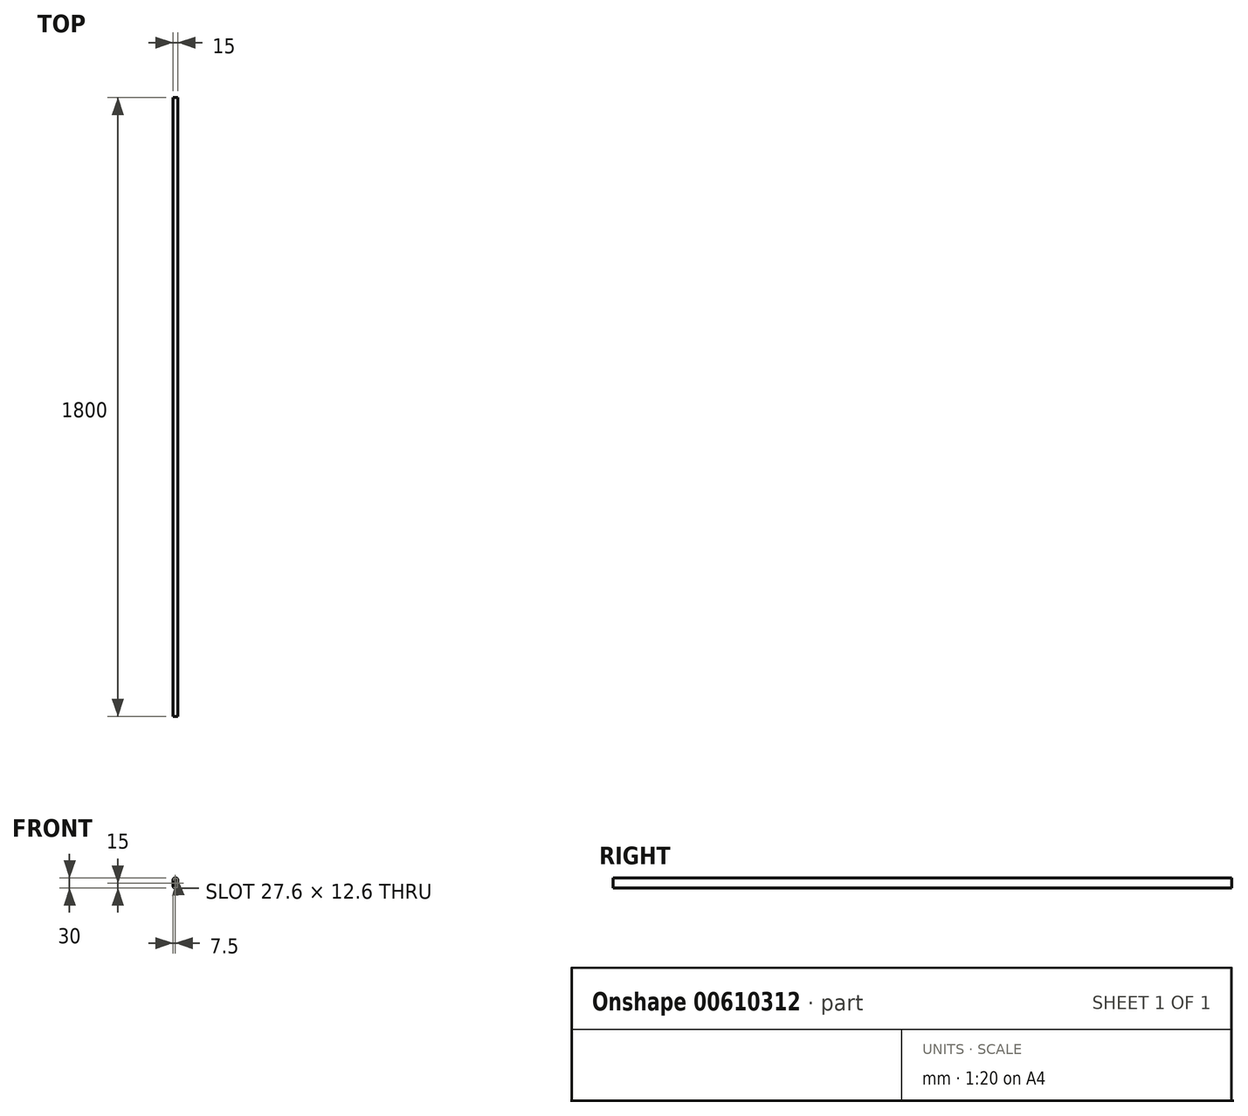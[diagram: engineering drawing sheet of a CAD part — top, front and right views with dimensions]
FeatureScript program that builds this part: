
annotation { "Feature Type Name" : "Feature", "Feature Type Description" : "" }
export const myFeature = defineFeature(function(context is Context, id is Id, definition is map)
    precondition{}
    {
        {
            var Q0;
            Q0=qCreatedBy(makeId("Front.planeOp"),FACE);
            var sketch = newSketch(context, id + "F0", { "sketchPlane" : qUnion([Q0])});
            skLineSegment(sketch, "E0.bottom", {"start": v(0, 15) * mm, "end": v(0, 15) * mm});
            skLineSegment(sketch, "E0.top", {"start": v(0, -15) * mm, "end": v(0, -15) * mm});
            skLineSegment(sketch, "E0.left", {"start": v(-7.5, 7.5) * mm, "end": v(-7.5, -7.5) * mm});
            skLineSegment(sketch, "E0.right", {"start": v(7.5, 7.5) * mm, "end": v(7.5, -7.5) * mm});
            skLineSegment(sketch, "E1", {"start": v(0, 0) * mm, "end": v(0, 15) * mm, "construction": true});
            skLineSegment(sketch, "E2", {"start": v(0, 0) * mm, "end": v(-7.5, 0) * mm, "construction": true});
            skPoint(sketch, "E3.visualSharp", {"position": v(-7.5, 15) * mm});
            skArc(sketch, "E3.filletArc", {"start": v(0, 15) * mm, "mid": v(-5.3, 12.8) * mm, "end": v(-7.5, 7.5) * mm});
            skPoint(sketch, "E4.visualSharp", {"position": v(7.5, 15) * mm});
            skArc(sketch, "E4.filletArc", {"start": v(7.5, 7.5) * mm, "mid": v(5.3, 12.8) * mm, "end": v(0, 15) * mm});
            skPoint(sketch, "E5.visualSharp", {"position": v(-7.5, -15) * mm});
            skArc(sketch, "E5.filletArc", {"start": v(-7.5, -7.5) * mm, "mid": v(-5.3, -12.8) * mm, "end": v(0, -15) * mm});
            skPoint(sketch, "E6.visualSharp", {"position": v(7.5, -15) * mm});
            skArc(sketch, "E6.filletArc", {"start": v(0, -15) * mm, "mid": v(5.3, -12.8) * mm, "end": v(7.5, -7.5) * mm});
            skSolve(sketch);
        }
        {
            var Q0;
            Q0=makeQuery(id+"F0.imprint","IMPRINT",FACE,{"disambiguationData":[TD([[makeQuery(id+"F0.imprint","IMPRINT",EDGE,{"derivedFrom":sQuery(id+"F0.wireOp",EDGE,"E1")}),1.0]])]});
            var Q1;
            Q1=makeQuery(id+"F0.imprint","IMPRINT",FACE,{"disambiguationData":[TD([[makeQuery(id+"F0.imprint","IMPRINT",EDGE,{"derivedFrom":sQuery(id+"F0.wireOp",EDGE,"E0.right")}),-1.0]])]});
            extrude(context, id + "F1", {"entities" : qUnion([Q0, Q1]), "depth" : 1800 * mm, "offsetDistance" : 25 * mm});
        }
        {
            var Q0;
            Q0=makeQuery(id+"F1.opExtrude","CAP_FACE",FACE,{"disambiguationData":[OSD([sQuery(id+"F0.wireOp",EDGE,"E0.left"),sQuery(id+"F0.wireOp",EDGE,"E0.right"),sQuery(id+"F0.wireOp",EDGE,"E3.filletArc"),sQuery(id+"F0.wireOp",EDGE,"E4.filletArc"),sQuery(id+"F0.wireOp",EDGE,"E5.filletArc"),sQuery(id+"F0.wireOp",EDGE,"E6.filletArc")])],"isStart":false});
            var Q1;
            Q1=makeQuery(id+"F1.opExtrude","CAP_FACE",FACE,{"disambiguationData":[OSD([sQuery(id+"F0.wireOp",EDGE,"E0.left"),sQuery(id+"F0.wireOp",EDGE,"E0.right"),sQuery(id+"F0.wireOp",EDGE,"E3.filletArc"),sQuery(id+"F0.wireOp",EDGE,"E4.filletArc"),sQuery(id+"F0.wireOp",EDGE,"E5.filletArc"),sQuery(id+"F0.wireOp",EDGE,"E6.filletArc")])],"isStart":true});
            var Q2;
            Q2=makeQuery(id+"F1.opExtrude","SWEPT_BODY",BODY,{"disambiguationData":[OSD([sQuery(id+"F0.wireOp",EDGE,"E0.left"),sQuery(id+"F0.wireOp",EDGE,"E0.right"),sQuery(id+"F0.wireOp",EDGE,"E3.filletArc"),sQuery(id+"F0.wireOp",EDGE,"E4.filletArc"),sQuery(id+"F0.wireOp",EDGE,"E5.filletArc"),sQuery(id+"F0.wireOp",EDGE,"E6.filletArc")])]});
            shell(context, id + "F2", {"entities" : qUnion([Q0, Q1]), "parts" : qUnion([Q2]), "thickness" : 1.2 * mm});
        }
    });
